# Revit family: LEAF_Slim_595_VIZULO
name_source: partatom
category: Lighting Fixtures
units: mm (PartAtom-declared; Revit-internal decimal feet)

## family parameters
Always vertical = Yes
Cut with Voids When Loaded = No
Light Source = Yes
OmniClass Number = 23.80.70.00
OmniClass Title = Lighting
Part Type = Normal
Room Calculation Point = No
Round Connector Dimension = Use Diameter
Shared = No
Work Plane-Based = No

## types (9) — shared parameters
Color Filter = 16777215
Dimming Lamp Color Temperature Shift = <None>
Emit Shape Visible in Rendering = No
Emit from Rectangle Length = 595 mm  [stored 1.9521 ft]
Emit from Rectangle Width = 595 mm  [stored 1.9521 ft]
Light Source Symbol Size = 610 mm
zero-valued in all types: Default Elevation

## type names (no varying parameters)
- 26 W, 3000 K
- 35 W, 3000 K
- 35 W, 4000 K
- 36 W, 3000 K
- 36 W, 4000 K
- 37 W, 3000 K
- 37 W, 4000 K
- 41 W, 3000 K
- 41 W, 4000 K

note: [stored X ft] marks values corroborated as IEEE doubles in the binary element streams (Revit-internal decimal feet)

## geometry (parser evidence)
native form markers: Sweep x3
no freeform markers — native parametric forms only
